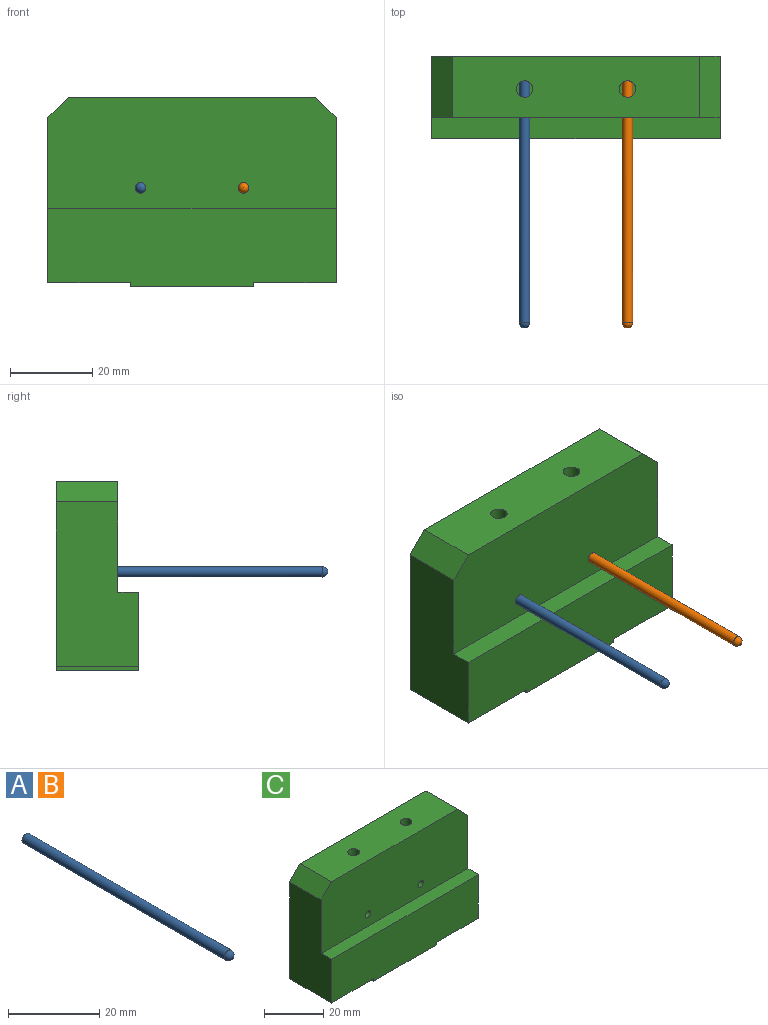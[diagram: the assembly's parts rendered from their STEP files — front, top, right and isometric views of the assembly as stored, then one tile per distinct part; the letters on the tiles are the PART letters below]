
ASSEMBLY  parts=3 mates=1
PART A: 3 faces, bbox 2.5x64x2.5 mm
  f0: cylinder r=1.25mm len=62.75mm, axis (0,1,0), area 492.8mm2, adj f1,f2
  f1: plane 2.5x2.5mm, normal (0,1,0), area 4.9mm2, adj f0
  f2: sphere r=1.25mm, area 9.8mm2, adj f0
PART B: same geometry as A
PART C: 24 faces, bbox 70x20x46 mm
  f0: plane 40x20mm, normal (-1,0,0), area 690mm2, adj f1,f4,f7,f10,f11,f23
  f1: plane 70x19mm, normal (0,-1,0), area 1290mm2, adj f0,f2,f3,f10,f20,f21,f22,f23
  f2: plane 30x20mm, normal (0,0,-1), area 600mm2, adj f1,f4,f21,f22
  f3: plane 40x20mm, normal (1,0,0), area 690mm2, adj f1,f4,f8,f10,f11,f20
  f4: plane 70x46mm, normal (0,1,0), area 3155mm2, adj f0,f2,f3,f7,f8,f9,f20,f21
  f5: plane 3.04x0.7mm, normal (0,0,1), area 1.5mm2, adj f12,f18
  f6: plane 3.04x0.7mm, normal (0,0,1), area 1.5mm2, adj f14,f16
  f7: plane 15x5mm, normal (-0.71,0,0.71), area 106.1mm2, adj f0,f4,f9,f11
  f8: plane 15x5mm, normal (0.71,0,0.71), area 106.1mm2, adj f3,f4,f9,f11
  f9: plane 60x15mm, normal (0,0,1), area 874.9mm2, adj f4,f7,f8,f11,f12,f14
  f10: plane 70x5mm, normal (0,0,1), area 350mm2, adj f0,f1,f3,f11
  f11: plane 70x27mm, normal (0,-1,0), area 1854.4mm2, adj f0,f3,f7,f8,f9,f10,f16,f18
  f12: cylinder r=2mm len=22mm, axis (0,0,1), area 270.8mm2, adj f5,f9,f13,f18
  f13: plane 3.04x0.7mm, normal (0,0,1), area 1.5mm2, adj f12,f18
  f14: cylinder r=2mm len=22mm, axis (0,0,1), area 270.8mm2, adj f6,f9,f15,f16
  f15: plane 3.04x0.7mm, normal (0,0,1), area 1.5mm2, adj f14,f16
  f16: cylinder r=1.3mm len=13mm, axis (0,-1,0), area 91.7mm2, adj f6,f11,f14,f15,f17
  f17: plane 2.6x2.6mm, normal (0,-1,0), area 5.3mm2, adj f16
  f18: cylinder r=1.3mm len=13mm, axis (0,-1,0), area 91.7mm2, adj f5,f11,f12,f13,f19
  f19: plane 2.6x2.6mm, normal (0,-1,0), area 5.3mm2, adj f18
  f20: plane 20x20mm, normal (0,0,-1), area 400mm2, adj f1,f3,f4,f21
  f21: plane 20x1mm, normal (1,0,0), area 20mm2, adj f1,f2,f4,f20
  f22: plane 20x1mm, normal (-1,0,0), area 20mm2, adj f1,f2,f4,f23
  f23: plane 20x20mm, normal (0,0,-1), area 400mm2, adj f0,f1,f4,f22
PLACE A t=(19.02,54.25,43.08)mm
PLACE B t=(44.02,54.25,43.08)mm
PLACE C t=(-3.48,56.25,19.08)mm
MATE parallel A.f0 <-> C.f18  axis (0,1,0) through (19.02,54.25,43.08)mm
